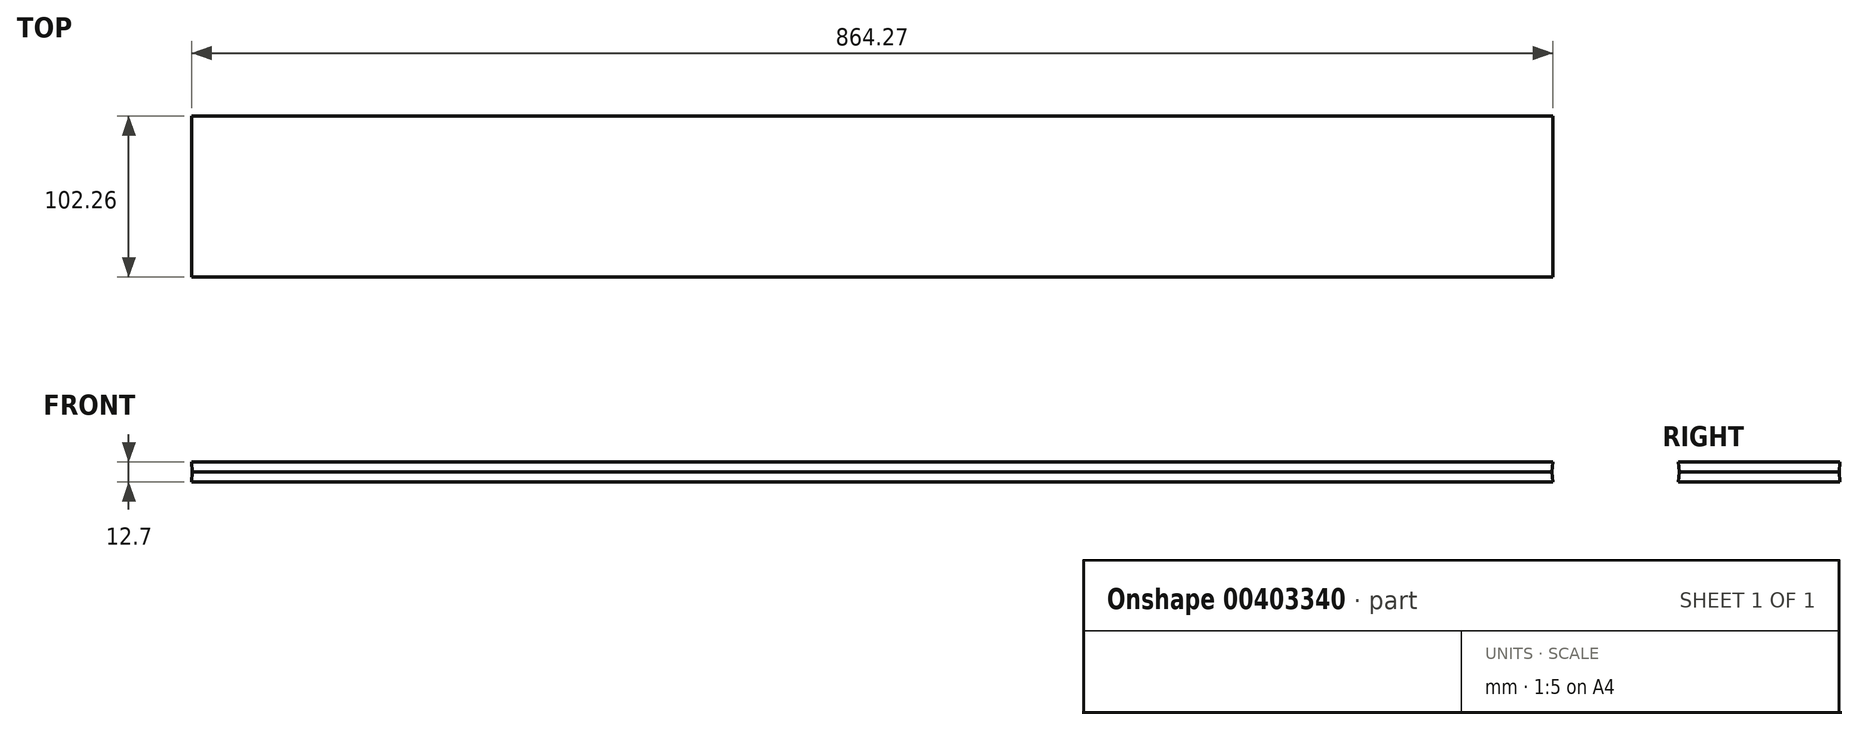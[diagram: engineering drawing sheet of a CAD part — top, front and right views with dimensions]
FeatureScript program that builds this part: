
annotation { "Feature Type Name" : "Feature", "Feature Type Description" : "" }
export const myFeature = defineFeature(function(context is Context, id is Id, definition is map)
    precondition{}
    {
        {
            var Q0;
            Q0=qCreatedBy(makeId("Top.planeOp"),FACE);
            var sketch = newSketch(context, id + "F0", { "sketchPlane" : qUnion([Q0])});
            skLineSegment(sketch, "E0.bottom", {"start": v(-372, 123.3) * mm, "end": v(491.6, 123.3) * mm});
            skLineSegment(sketch, "E0.top", {"start": v(-372, 21.7) * mm, "end": v(491.6, 21.7) * mm});
            skLineSegment(sketch, "E0.left", {"start": v(-372, 123.3) * mm, "end": v(-372, 21.7) * mm});
            skLineSegment(sketch, "E0.right", {"start": v(491.6, 123.3) * mm, "end": v(491.6, 21.7) * mm});
            skSolve(sketch);
        }
        {
            var Q0;
            Q0=makeQuery(id+"F0.imprint","IMPRINT",FACE,{"disambiguationData":[TD([[makeQuery(id+"F0.imprint","IMPRINT",EDGE,{"derivedFrom":sQuery(id+"F0.wireOp",EDGE,"E0.bottom")}),-1.0]])]});
            var Q1;
            Q1=sQuery(id+"F0.wireOp",EDGE,"E0.right");
            var Q2;
            Q2=sQuery(id+"F0.wireOp",EDGE,"E0.top");
            extrude(context, id + "F1", {"entities" : qUnion([Q0]), "surfaceEntities" : qUnion([Q1, Q2]), "endBound" : BoundingType.SYMMETRIC, "depth" : 12.7 * mm, "hasDraft" : true, "draftAngle" : 3 * degree});
        }
    });
